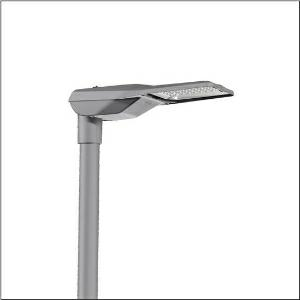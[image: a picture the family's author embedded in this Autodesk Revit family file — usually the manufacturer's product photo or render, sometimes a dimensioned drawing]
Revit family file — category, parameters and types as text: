
# Revit family: streetlight_sl_21_mini___st0_8a_5xe2c43s08jb_ad40
name_source: partatom
category: Lighting Fixtures
units: mm (PartAtom-declared; Revit-internal decimal feet)

## family parameters
Cut with Voids When Loaded = No
Host = Face
Light Source = No
Part Type = Normal
Room Calculation Point = No
Round Connector Dimension = Use Diameter
Shared = No

## types (1)
- --- (1 x LED, 13500 lm, 88.6 W, 4000K)
    Apparent Load = 89 VA
    CIE Flux Codes = 41 75 97 100 100
    Color Rendering = 70
    Color Temperature = 4000K
    Default Elevation = 1800 mm
    Description = Streetlight SL 21 mini, mast luminaire, primary light control with lens, of PMMA, primary optical cover: cover, of toughened safety glass, transparent, light distribution: ST0.8a, light emission: direct distribution, primary light characteristic: asymmetric, installation type: side-entry, post-top, LED, High Power LED, rated luminous flux: 13.500lm, luminous efficacy: 152lm/W, light colour: 740, colour temperature: 4000K, control gear: D4i, control: overheat protection, constant luminous flux control, time-dependent luminous flux control, flexible luminous flux parameterisation, pre-setting: logarithmic dimming characteristic, mains connection: 220..240V, AC, 50/60Hz, start of lifetime: 89W, end of service life: 92W, reduction: 41W, luminaire housing, of diecast aluminium, powder-coated, SITECO metallic grey (DB 702S), corrosivity category C5 high according to DIN EN ISO 12944, please order mast flange separately, inclination adjustable: 0°, 5°, 10°, 15°, sealing non-destructively replaceable, multi-level sealing system, length: 628mm, width: 235mm, height: 110mm, mast flange for spigot size: 42mm (side-entry): 5XC10008XM4, 60/48mm (side-entry/post-top): 5XC10108XM2, 76/60mm (side-entry/post-top): 5XC10108XM1, mounting height: 4..8m, Smart Interface above, protection rating (complete): IP66, insulation class (complete): insulation class II (safety insulation), certification: CE, ENEC, ENEC+, VDE, impact resistance: IK10, permissible operating ambient temperature for outdoor applications: -40..+50°C, standard-compliant lighting for roads and squares, packaging unit: 1 piece

Light Distribution: ST0.8a
    Height = 110 mm
    Lamp = 1 x LED
    Lamp Light Flux = 13500 lm
    Lamp Power = 88.6 W
    Lamp count = 1
    Length = 625 mm
    Luminous efficacy = 152 lm/W
    Manufacturer = Siteco
    ModVariant = No
    Model = 5XE2C43S08JB
    Number of Poles = 1
    OnlyDefault = Yes
    Power Factor = 1
    Product Name = Streetlight SL 21 mini | ST0.8a
    Product group = mast luminaire | pylon top
    ProductGroupID = 6100
    Protection Class = Protection class II
    Protection Degree = IP 66
    RLX_Detail_Level = 1
    RLX_Emergency_Light_Flux = 0 lm
    RLX_Emergency_Type = 0
    RLX_Emergency_Type_DB = No
    RlxData = <blob elided: 26153 chars, md5=ea3c1aab>
    Socket = socket
    Standby Power = 0 W
    System Light Flux = 13500 lm
    System Power = 89 W
    Type Comments = factory setting: luminous flux: 100 % | dim-lin: 254 | 915 mA
    Type Image = l_1003515.jpg
    URL = http://relux.com
    VarID = @adj_030817
    Voltage = 0 V
    Weight = 0.00 kg
    Width = 234 mm

## geometry (parser evidence)
native form markers: Blend x4, Sweep x13
no freeform markers — native parametric forms only
